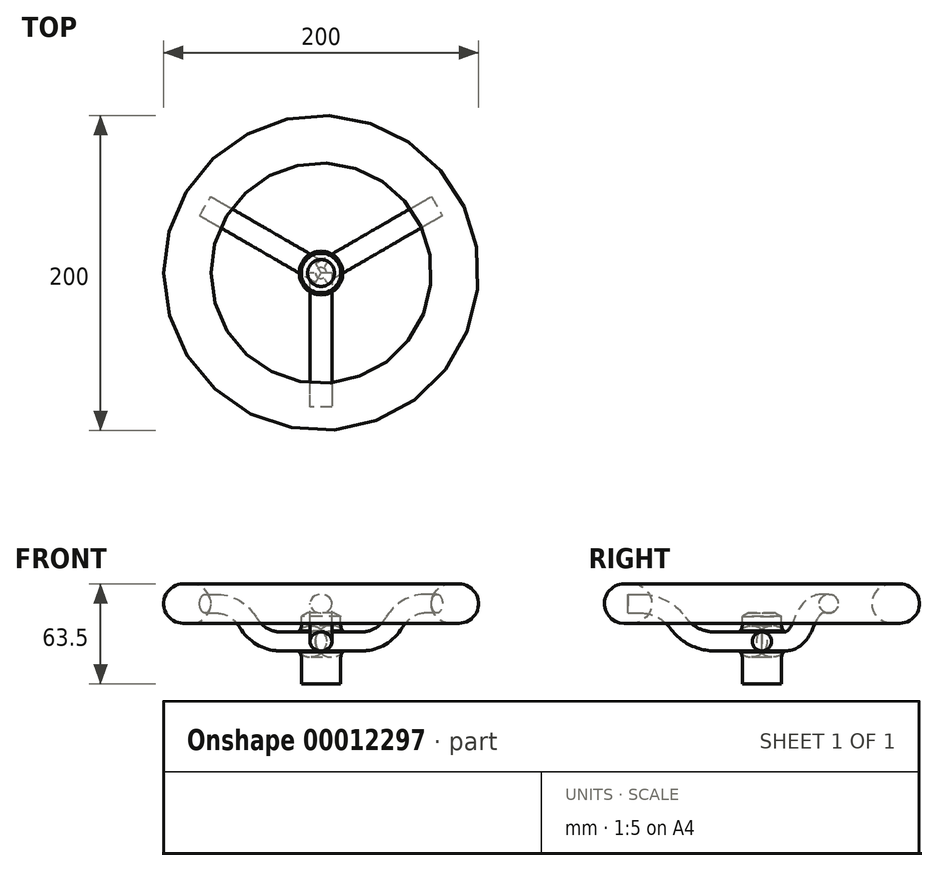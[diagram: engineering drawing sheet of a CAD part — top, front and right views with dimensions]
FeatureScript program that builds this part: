
annotation { "Feature Type Name" : "Feature", "Feature Type Description" : "" }
export const myFeature = defineFeature(function(context is Context, id is Id, definition is map)
    precondition{}
    {
        {
            var Q0;
            Q0=qCreatedBy(makeId("Right.planeOp"),FACE);
            var sketch = newSketch(context, id + "F0", { "sketchPlane" : qUnion([Q0])});
            skLineSegment(sketch, "E0.bottom", {"start": v(0, 0) * mm, "end": v(-12.5, 0) * mm});
            skLineSegment(sketch, "E0.top", {"start": v(0, 45) * mm, "end": v(-12.5, 45) * mm});
            skLineSegment(sketch, "E0.right", {"start": v(-12.5, 0) * mm, "end": v(-12.5, 16.8) * mm});
            skArc(sketch, "E1", {"start": v(-13.83, 33.8) * mm, "mid": v(-16.5, 27) * mm, "end": v(-13.83, 20.2) * mm});
            skLineSegment(sketch, "E2.trimOffspring", {"start": v(-12.5, 37.2) * mm, "end": v(-12.5, 45) * mm});
            skLineSegment(sketch, "E3", {"start": v(0, 45) * mm, "end": v(0, 0) * mm});
            skPoint(sketch, "E4.visualSharp", {"position": v(-12.5, 35) * mm});
            skArc(sketch, "E4.filletArc", {"start": v(-13.83, 33.8) * mm, "mid": v(-12.85, 35.37) * mm, "end": v(-12.5, 37.2) * mm});
            skPoint(sketch, "E5.visualSharp", {"position": v(-12.5, 19) * mm});
            skArc(sketch, "E5.filletArc", {"start": v(-12.5, 16.8) * mm, "mid": v(-12.85, 18.63) * mm, "end": v(-13.83, 20.2) * mm});
            skSolve(sketch);
        }
        {
            var Q0;
            Q0 = qSketchRegion(id + "F0", true);
            var Q1;
            Q1=sQuery(id+"F0.wireOp",EDGE,"E3");
            revolve(context, id + "F1", {"entities" : qUnion([Q0]), "axis" : qUnion([Q1]), "revolveType" : RevolveType.FULL});
        }
        {
            var Q0;
            Q0=qCreatedBy(makeId("Right.planeOp"),FACE);
            var sketch = newSketch(context, id + "F2", { "sketchPlane" : qUnion([Q0])});
            skLineSegment(sketch, "E6", {"start": v(0, -13.3) * mm, "end": v(0, 61.57) * mm, "construction": true});
            skSolve(sketch);
        }
        {
            var Q0;
            Q0=qCreatedBy(makeId("Right.planeOp"),FACE);
            var sketch = newSketch(context, id + "F3", { "sketchPlane" : qUnion([Q0])});
            skArc(sketch, "E7", {"start": v(-82.5, 38.5) * mm, "mid": v(-70, 51) * mm, "end": v(-82.5, 63.5) * mm});
            skArc(sketch, "E8.0.MirrorC", {"start": v(-87.5, 38.5) * mm, "mid": v(-100, 51) * mm, "end": v(-87.5, 63.5) * mm});
            skLineSegment(sketch, "E9.bottom", {"start": v(-87.5, 63.5) * mm, "end": v(-82.5, 63.5) * mm});
            skLineSegment(sketch, "E9.top", {"start": v(-87.5, 38.5) * mm, "end": v(-82.5, 38.5) * mm});
            skLineSegment(sketch, "E10", {"start": v(-82.5, 51) * mm, "end": v(-104.34, 51) * mm, "construction": true});
            skLineSegment(sketch, "E11", {"start": v(-85, 63.5) * mm, "end": v(-85, 38.5) * mm, "construction": true});
            skPoint(sketch, "E12.orphan", {"position": v(-70, 51) * mm});
            skPoint(sketch, "E13", {"position": v(0, 0) * mm});
            skPoint(sketch, "E14", {"position": v(-85, 51) * mm});
            skSolve(sketch);
        }
        {
            var Q0;
            Q0 = qSketchRegion(id + "F3", true);
            var Q1;
            Q1=sQuery(id+"F2.wireOp",EDGE,"E6");
            revolve(context, id + "F4", {"entities" : qUnion([Q0]), "axis" : qUnion([Q1]), "revolveType" : RevolveType.FULL});
        }
        {
            var Q0;
            Q0=qCreatedBy(makeId("Right.planeOp"),FACE);
            var sketch = newSketch(context, id + "F5", { "sketchPlane" : qUnion([Q0])});
            skLineSegment(sketch, "E15", {"start": v(-76.99, 51) * mm, "end": v(-85, 51) * mm});
            skLineSegment(sketch, "E16", {"start": v(0, 27) * mm, "end": v(-30, 27) * mm});
            skArc(sketch, "E17", {"start": v(-30, 27) * mm, "mid": v(-43.2, 30.17) * mm, "end": v(-53.5, 39) * mm});
            skArc(sketch, "E18", {"start": v(-53.5, 39) * mm, "mid": v(-63.8, 47.83) * mm, "end": v(-76.99, 51) * mm});
            skSolve(sketch);
        }
        {
            var Q0;
            Q0=qCreatedBy(makeId("Front.planeOp"),FACE);
            var sketch = newSketch(context, id + "F6", { "sketchPlane" : qUnion([Q0])});
            skEllipse(sketch, "E19", {"center": v(0, 27) * mm, "majorRadius": 7 * mm, "minorRadius": 6 * mm, "majorAxis": v(1, 0)});
            skSolve(sketch);
        }
        {
            var Q0;
            Q0=makeQuery(id+"F6.imprint","IMPRINT",FACE,{"disambiguationData":[TD([[makeQuery(id+"F6.imprint","IMPRINT",EDGE,{"derivedFrom":sQuery(id+"F6.wireOp",EDGE,"E19")}),1.0]])]});
            var Q1;
            Q1=sQuery(id+"F5.wireOp",EDGE,"E16");
            var Q2;
            Q2=sQuery(id+"F5.wireOp",EDGE,"E17");
            var Q3;
            Q3=sQuery(id+"F5.wireOp",EDGE,"E18");
            var Q4;
            Q4=sQuery(id+"F5.wireOp",EDGE,"E15");
            sweep(context, id + "F7", {"profiles" : qUnion([Q0]), "path" : qUnion([Q1, Q2, Q3, Q4])});
        }
        {
            var Q0;
            Q0=makeQuery(id+"F1.opRevolve","SWEPT_EDGE",EDGE,{"disambiguationData":[OSD([sQuery(id+"F0.wireOp",EDGE,"E0.top"),sQuery(id+"F0.wireOp",EDGE,"E2.trimOffspring")])]});
            chamfer(context, id + "F8", {"entities" : qUnion([Q0]), "chamferType" : ChamferType.TWO_OFFSETS, "width1" : 4 * mm, "oppositeDirection" : false, "width2" : 2 * mm, "tangentPropagation" : true});
        }
        {
            var Q0;
            Q0=makeQuery(id+"F7.opSweep","SWEPT_BODY",BODY,{"disambiguationData":[OSD([sQuery(id+"F5.wireOp",EDGE,"E15"),sQuery(id+"F6.wireOp",EDGE,"E19")])]});
            var Q1;
            Q1=sQuery(id+"F2.wireOp",EDGE,"E6");
            circularPattern(context, id + "F9", {"entities" : qUnion([Q0]), "axis" : qUnion([Q1]), "angle" : 360 * degree, "instanceCount" : 3, "equalSpace" : true});
        }
    });
